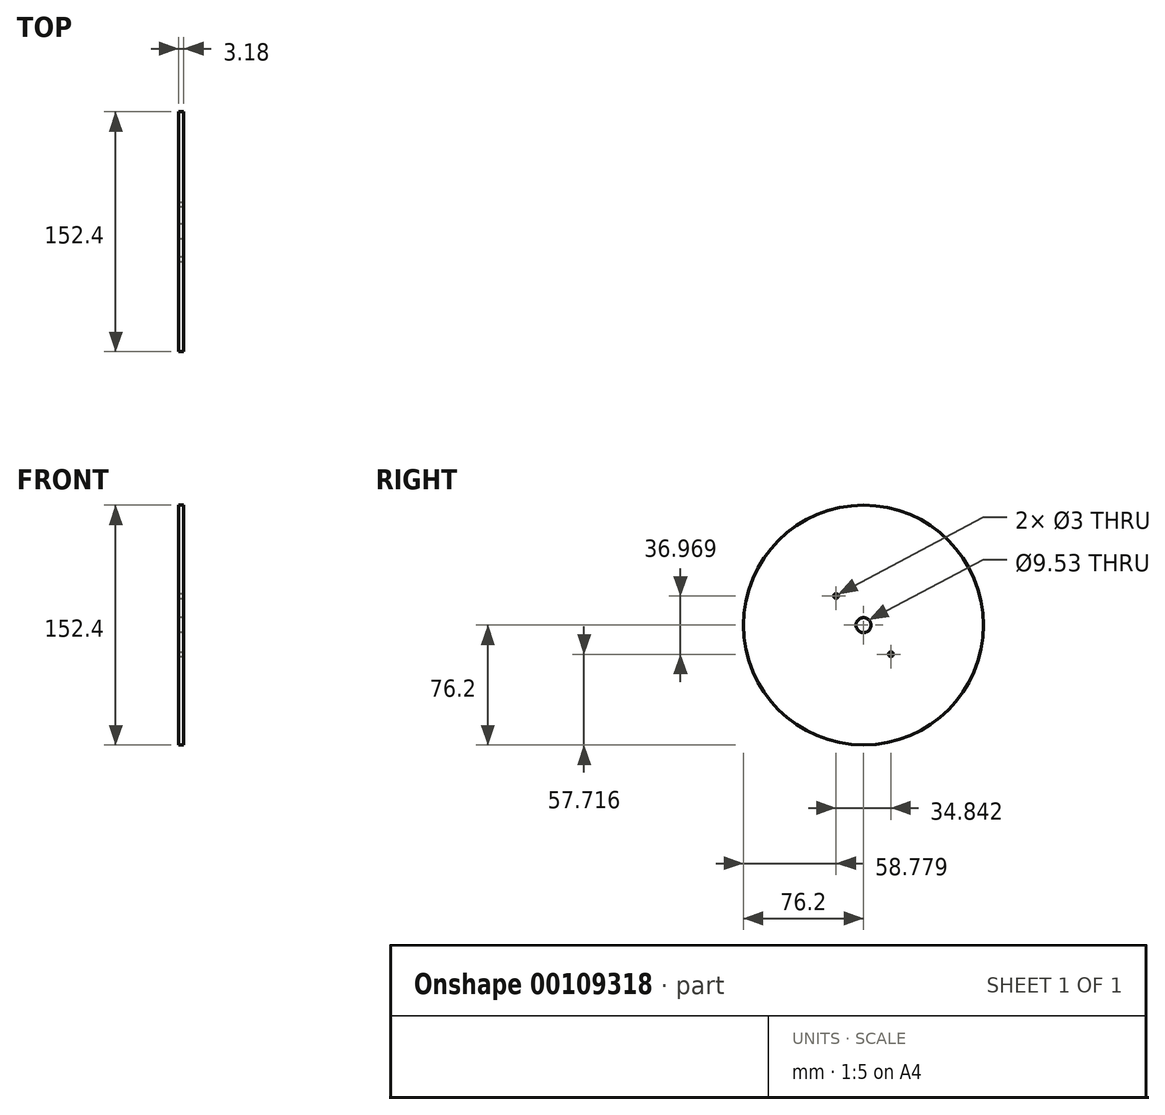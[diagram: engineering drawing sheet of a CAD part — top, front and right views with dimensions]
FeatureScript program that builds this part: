
annotation { "Feature Type Name" : "Feature", "Feature Type Description" : "" }
export const myFeature = defineFeature(function(context is Context, id is Id, definition is map)
    precondition{}
    {
        {
            var Q0;
            Q0=qCreatedBy(makeId("Right.planeOp"),FACE);
            var sketch = newSketch(context, id + "F0", { "sketchPlane" : qUnion([Q0])});
            skCircle(sketch, "E0", {"center": v(0, 0) * mm, "radius": 76.2 * mm});
            skCircle(sketch, "E1", {"center": v(0, 0) * mm, "radius": 4.76 * mm});
            skSolve(sketch);
        }
        {
            var Q0;
            Q0=makeQuery(id+"F0.imprint","IMPRINT",FACE,{"disambiguationData":[TD([[makeQuery(id+"F0.imprint","IMPRINT",EDGE,{"derivedFrom":sQuery(id+"F0.wireOp",EDGE,"E0")}),1.0]])]});
            extrude(context, id + "F1", {"entities" : qUnion([Q0]), "depth" : 3.17 * mm});
        }
        {
            var Q0;
            Q0=makeQuery(id+"F1.opExtrude","CAP_FACE",FACE,{"disambiguationData":[OSD([sQuery(id+"F0.wireOp",EDGE,"E0")])],"isStart":false});
            var sketch = newSketch(context, id + "F2", { "sketchPlane" : qUnion([Q0])});
            skCircle(sketch, "E2", {"center": v(0, 0) * mm, "radius": 1.59 * mm});
            skSolve(sketch);
        }
        {
            var Q0;
            Q0=makeQuery(id+"F2.imprint","IMPRINT",FACE,{"disambiguationData":[TD([[makeQuery(id+"F2.imprint","IMPRINT",EDGE,{"derivedFrom":sQuery(id+"F2.wireOp",EDGE,"E2")}),1.0]])]});
            extrude(context, id + "F3", {"entities" : qUnion([Q0]), "operationType" : NewBodyOperationType.REMOVE, "endBound" : BoundingType.THROUGH_ALL, "oppositeDirection" : true, "depth" : 25.4 * mm});
        }
        {
            var Q0;
            Q0=makeQuery(id+"F1.opExtrude","CAP_FACE",FACE,{"disambiguationData":[OSD([sQuery(id+"F0.wireOp",EDGE,"E0")])],"isStart":false});
            var sketch = newSketch(context, id + "F4", { "sketchPlane" : qUnion([Q0])});
            skLineSegment(sketch, "E3", {"start": v(-52.26, 55.45) * mm, "end": v(0, 0) * mm, "construction": true});
            skLineSegment(sketch, "E4", {"start": v(0, 0) * mm, "end": v(52.26, -55.45) * mm, "construction": true});
            skLineSegment(sketch, "E5", {"start": v(0, 0) * mm, "end": v(-55.45, -52.26) * mm, "construction": true});
            skLineSegment(sketch, "E6", {"start": v(0, 0) * mm, "end": v(55.45, 52.26) * mm, "construction": true});
            skCircle(sketch, "E7", {"center": v(-17.42, 18.48) * mm, "radius": 1.5 * mm});
            skCircle(sketch, "E8", {"center": v(17.42, -18.48) * mm, "radius": 1.5 * mm});
            skSolve(sketch);
        }
        {
            var Q0;
            Q0 = qSketchRegion(id + "F4", true);
            extrude(context, id + "F5", {"entities" : qUnion([Q0]), "operationType" : NewBodyOperationType.REMOVE, "oppositeDirection" : true, "depth" : 25.4 * mm});
        }
    });
